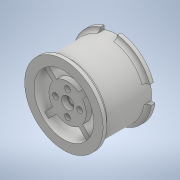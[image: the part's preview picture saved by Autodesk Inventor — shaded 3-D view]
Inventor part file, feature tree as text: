
AUTODESK INVENTOR PART (.ipt)
format: ipt  version: 2020 (Build 240168000, 168)  size: 384,000 bytes
history: native  units: mm
features: extrude x8, sketch x7, projected_geometry x4, other x1, revolve x1
ambient origin geometry x8: Origin, YZ Plane, XZ Plane, XY Plane, X Axis, Y Axis, Z Axis, Center Point
bodies: Body1 (feature_tree)
feature tree (21):
  other  "Твердое тело1"
  revolve  "Вращение1"
  extrude  "Выдавливание1"  Depth=16.0mm
  sketch  "Эскиз3"
  extrude  "Выдавливание2"  Depth=12.0mm
  extrude  "Выдавливание3"  Depth=28.0mm
  extrude  "Выдавливание5"  Depth=5.0mm
  extrude  "Выдавливание6"  Depth=2.0mm
  extrude  "Выдавливание8"  Depth=2.0mm
  extrude  "Выдавливание9"  TaperAngle=360.0deg  [1 undecoded]
  extrude  "Выдавливание10"  Depth=20.0mm
  sketch  "Эскиз4"
  sketch  "Эскиз8"
  projected_geometry  "Спроецированная петля2"
  sketch  "Эскиз9"
  sketch  "Эскиз11"
  projected_geometry  "Спроецированная петля5"
  projected_geometry  "Спроецированная петля6"
  projected_geometry  "Спроецированная петля7"
  sketch  "Эскиз12"
  sketch  "Эскиз13"
note: 1 required parameter value undecoded (feature->parameter linkage not recoverable at this tier; creation-order binding heuristic only, values carry confidence <= 0.55)
